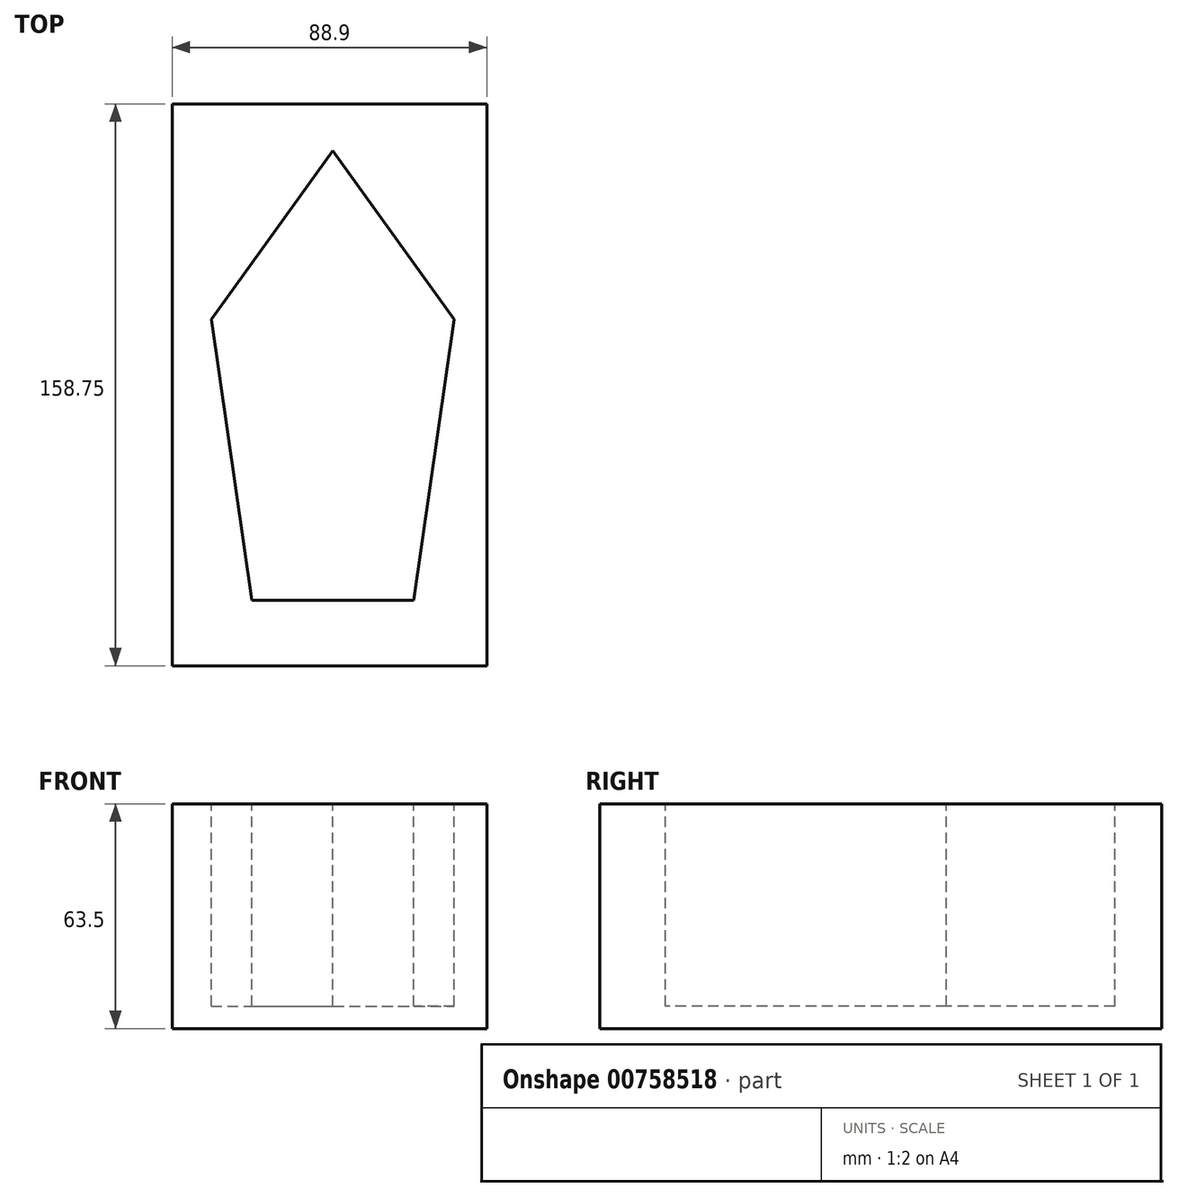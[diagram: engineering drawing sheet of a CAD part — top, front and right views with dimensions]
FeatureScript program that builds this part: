
annotation { "Feature Type Name" : "Feature", "Feature Type Description" : "" }
export const myFeature = defineFeature(function(context is Context, id is Id, definition is map)
    precondition{}
    {
        {
            var Q0;
            Q0=qCreatedBy(makeId("Top.planeOp"),FACE);
            var sketch = newSketch(context, id + "F0", { "sketchPlane" : qUnion([Q0])});
            skLineSegment(sketch, "E0.bottom", {"start": v(-61.97, 87.24) * mm, "end": v(26.93, 87.24) * mm});
            skLineSegment(sketch, "E0.top", {"start": v(-61.97, -71.51) * mm, "end": v(26.93, -71.51) * mm});
            skLineSegment(sketch, "E0.left", {"start": v(-61.97, 87.24) * mm, "end": v(-61.97, -71.51) * mm});
            skLineSegment(sketch, "E0.right", {"start": v(26.93, 87.24) * mm, "end": v(26.93, -71.51) * mm});
            skSolve(sketch);
        }
        {
            var Q0;
            Q0=makeQuery(id+"F0.imprint","IMPRINT",FACE,{"disambiguationData":[TD([[makeQuery(id+"F0.imprint","IMPRINT",EDGE,{"derivedFrom":sQuery(id+"F0.wireOp",EDGE,"E0.bottom")}),-1.0]])]});
            extrude(context, id + "F1", {"entities" : qUnion([Q0]), "depth" : 63.5 * mm, "offsetDistance" : 25.4 * mm});
        }
        {
            var Q0;
            Q0=makeQuery(id+"F1.opExtrude","CAP_FACE",FACE,{"disambiguationData":[OSD([sQuery(id+"F0.wireOp",EDGE,"E0.bottom"),sQuery(id+"F0.wireOp",EDGE,"E0.top"),sQuery(id+"F0.wireOp",EDGE,"E0.left"),sQuery(id+"F0.wireOp",EDGE,"E0.right")])],"isStart":false});
            var sketch = newSketch(context, id + "F2", { "sketchPlane" : qUnion([Q0])});
            skLineSegment(sketch, "E1.bottom", {"start": v(-39.39, 40.9) * mm, "end": v(6.33, 40.9) * mm});
            skLineSegment(sketch, "E1.top", {"start": v(-39.39, -53.08) * mm, "end": v(6.33, -53.08) * mm});
            skLineSegment(sketch, "E1.left", {"start": v(-39.39, 40.9) * mm, "end": v(-39.39, -53.08) * mm});
            skLineSegment(sketch, "E1.right", {"start": v(6.33, 40.9) * mm, "end": v(6.33, -53.08) * mm});
            skLineSegment(sketch, "E2", {"start": v(-16.53, -53.08) * mm, "end": v(-16.53, 73.92) * mm});
            skLineSegment(sketch, "E3", {"start": v(-16.53, 73.92) * mm, "end": v(17.78, 26.4) * mm});
            skLineSegment(sketch, "E4", {"start": v(17.78, 26.4) * mm, "end": v(6.33, -53.08) * mm});
            skLineSegment(sketch, "E5", {"start": v(17.78, 26.4) * mm, "end": v(-50.9, 26.4) * mm});
            skLineSegment(sketch, "E6", {"start": v(-50.9, 26.4) * mm, "end": v(-16.53, 73.92) * mm});
            skLineSegment(sketch, "E7", {"start": v(-50.9, 26.4) * mm, "end": v(-39.39, -53.08) * mm});
            skSolve(sketch);
        }
        {
            var Q0;
            {var subQ0=sQuery(id+"F2.wireOp",EDGE,"E3");Q0=makeQuery(id+"F2.imprint","IMPRINT",FACE,{"disambiguationData":[TD([[makeQuery(id+"F2.imprint","IMPRINT",EDGE,{"derivedFrom":subQ0}),-1.0]])]});}
            var Q1;
            {var subQ0=sQuery(id+"F2.wireOp",EDGE,"E6");Q1=makeQuery(id+"F2.imprint","IMPRINT",FACE,{"disambiguationData":[TD([[makeQuery(id+"F2.imprint","IMPRINT",EDGE,{"derivedFrom":subQ0}),-1.0]])]});}
            var Q2;
            {var subQ0=sQuery(id+"F2.wireOp",EDGE,"E1.left");var subQ1=sQuery(id+"F2.wireOp",EDGE,"E1.bottom");var subQ2=makeQuery(id+"F2.imprint","INTERSECT",VERTEX,{"derivedFrom":[subQ1,subQ0]});Q2=makeQuery(id+"F2.imprint","IMPRINT",FACE,{"disambiguationData":[TD([[makeQuery(id+"F2.imprint","IMPRINT",EDGE,{"disambiguationData":[TD([[subQ2,-1.0]])],"derivedFrom":subQ1}),-1.0]])]});}
            var Q3;
            {var subQ0=sQuery(id+"F2.wireOp",EDGE,"E1.right");var subQ1=sQuery(id+"F2.wireOp",EDGE,"E1.bottom");var subQ2=makeQuery(id+"F2.imprint","INTERSECT",VERTEX,{"derivedFrom":[subQ1,subQ0]});Q3=makeQuery(id+"F2.imprint","IMPRINT",FACE,{"disambiguationData":[TD([[makeQuery(id+"F2.imprint","IMPRINT",EDGE,{"disambiguationData":[TD([[subQ2,1.0]])],"derivedFrom":subQ1}),-1.0]])]});}
            var Q4;
            {var subQ1=sQuery(id+"F2.wireOp",EDGE,"E1.top");var subQ3=sQuery(id+"F2.wireOp",EDGE,"E2");var subQ4=makeQuery(id+"F2.imprint","INTERSECT",VERTEX,{"derivedFrom":[subQ1,subQ3]});Q4=makeQuery(id+"F2.imprint","IMPRINT",FACE,{"disambiguationData":[TD([[makeQuery(id+"F2.imprint","IMPRINT",EDGE,{"disambiguationData":[TD([[subQ4,-1.0]])],"derivedFrom":subQ3}),-1.0]])]});}
            var Q5;
            {var subQ0=sQuery(id+"F2.wireOp",EDGE,"E4");Q5=makeQuery(id+"F2.imprint","IMPRINT",FACE,{"disambiguationData":[TD([[makeQuery(id+"F2.imprint","IMPRINT",EDGE,{"derivedFrom":subQ0}),-1.0]])]});}
            var Q6;
            {var subQ1=sQuery(id+"F2.wireOp",EDGE,"E1.top");var subQ3=sQuery(id+"F2.wireOp",EDGE,"E2");var subQ4=makeQuery(id+"F2.imprint","INTERSECT",VERTEX,{"derivedFrom":[subQ1,subQ3]});Q6=makeQuery(id+"F2.imprint","IMPRINT",FACE,{"disambiguationData":[TD([[makeQuery(id+"F2.imprint","IMPRINT",EDGE,{"disambiguationData":[TD([[subQ4,-1.0]])],"derivedFrom":subQ3}),1.0]])]});}
            var Q7;
            {var subQ0=sQuery(id+"F2.wireOp",EDGE,"E7");Q7=makeQuery(id+"F2.imprint","IMPRINT",FACE,{"disambiguationData":[TD([[makeQuery(id+"F2.imprint","IMPRINT",EDGE,{"derivedFrom":subQ0}),1.0]])]});}
            extrude(context, id + "F3", {"entities" : qUnion([Q0, Q1, Q2, Q3, Q4, Q5, Q6, Q7]), "operationType" : NewBodyOperationType.REMOVE, "oppositeDirection" : true, "depth" : 57.15 * mm, "offsetDistance" : 25.4 * mm});
        }
    });
